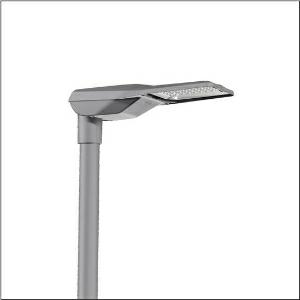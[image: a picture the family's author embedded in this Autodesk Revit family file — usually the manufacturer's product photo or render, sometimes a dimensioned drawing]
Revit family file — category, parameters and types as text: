
# Revit family: streetlight_sl_21_iq_mini___st1_0a_5xe2d31g08jb_707a
name_source: partatom
category: Lighting Fixtures
units: mm (PartAtom-declared; Revit-internal decimal feet)

## family parameters
Cut with Voids When Loaded = No
Host = Face
Light Source = No
Part Type = Normal
Room Calculation Point = No
Round Connector Dimension = Use Diameter
Shared = No

## types (1)
- --- (1 x LED, 10820 lm, 71.6 W, 3000K)
    Apparent Load = 72 VA
    CIE Flux Codes = 40 73 97 100 100
    Color Rendering = 70
    Color Temperature = 3000K
    Default Elevation = 1800 mm
    Description = Streetlight SL 21 iQ mini, mast luminaire, primary light control with lens, of PMMA, primary optical cover: cover, of toughened safety glass, transparent, light distribution: ST1.0a, light emission: direct distribution, primary light characteristic: asymmetric, installation type: post-top, side-entry, LED, High Power LED, rated luminous flux: 10.820lm, luminous efficacy: 151lm/W, light colour: 730, colour temperature: 3000K, control gear: iQ Street-Remote, control: Street-Remote, Auto-Match, Temp-Guard, Lumen-Switch, Night-Set, Smart-Wire, Light-Fading, Desk-Remote (wireless, voltage-free reading and setting of iQ features in the workshop via application-optimized NFC function/RFID function), optimised constant luminous flux control (CLO 2.0), pre-setting: linear dimming characteristic, mains connection: 220..240V, AC, 50/60Hz, start of lifetime: 72W, end of service life: 75W, reduction: 33W, luminaire housing, of diecast aluminium, powder-coated, Siteco® metallic grey (DB 702S), corrosivity category C5 mid according to DIN EN ISO 12944, please order mast flange separately, inclination adjustable: 0°, 5°, 10°, 15°, sealing non-destructively replaceable, multi-level sealing system, length: 628mm, width: 235mm, height: 110mm, mast flange for spigot size: 42mm (side-entry): 5XC10008XM4, 60/48mm (side-entry/post-top): 5XC10108XM2, 76/60mm (side-entry/post-top): 5XC10108XM1, mounting height: 4..8m, protection rating (complete): IP66, insulation class (complete): insulation class II (safety insulation), certification: CE, ENEC, ENEC+, VDE, impact resistance: IK10, permissible operating ambient temperature for outdoor applications: -40..+50°C, standard-compliant lighting for roads and squares, packaging unit: 1 piece

Light Distribution: ST1.0a
    Height = 110 mm
    Lamp = 1 x LED
    Lamp Light Flux = 10820 lm
    Lamp Power = 71.6 W
    Lamp count = 1
    Length = 625 mm
    Luminous efficacy = 151 lm/W
    Manufacturer = Siteco
    ModVariant = No
    Model = 5XE2D31G08JB
    Number of Poles = 1
    OnlyDefault = Yes
    Power Factor = 1
    Product Name = Streetlight SL 21 iQ mini | ST1.0a
    Product group = mast luminaire | pylon top
    ProductGroupID = 6100
    Protection Class = Protection class II
    Protection Degree = IP 66
    RLX_Detail_Level = 1
    RLX_Emergency_Light_Flux = 0 lm
    RLX_Emergency_Type = 0
    RLX_Emergency_Type_DB = No
    RlxData = <blob elided: 26333 chars, md5=10866a3b>
    Socket = socket
    Standby Power = 0 W
    System Light Flux = 10820 lm
    System Power = 72 W
    Type Comments = factory setting: luminous flux: 100 % | dim-lin: 254 | 746 mA
    Type Image = l_1003519.jpg
    URL = http://relux.com
    VarID = @adj_192627
    Voltage = 0 V
    Weight = 0.00 kg
    Width = 234 mm

## geometry (parser evidence)
native form markers: Blend x4, Sweep x11
no freeform markers — native parametric forms only
